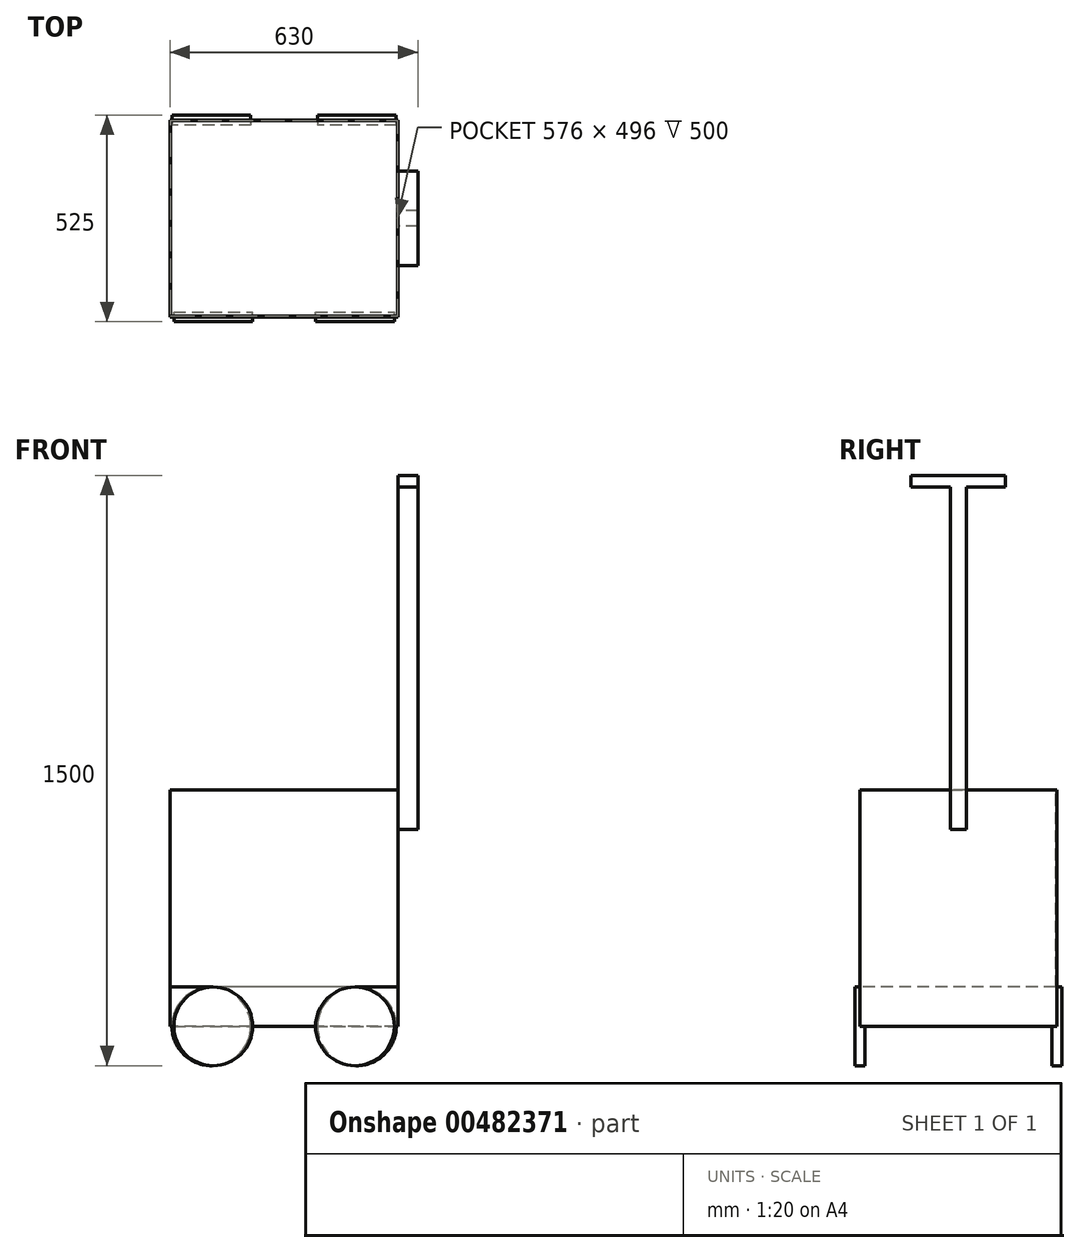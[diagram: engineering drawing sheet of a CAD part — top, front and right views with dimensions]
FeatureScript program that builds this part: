
annotation { "Feature Type Name" : "Feature", "Feature Type Description" : "" }
export const myFeature = defineFeature(function(context is Context, id is Id, definition is map)
    precondition{}
    {
        {
            var Q0;
            Q0=qCreatedBy(makeId("Front.planeOp"),FACE);
            var sketch = newSketch(context, id + "F0", { "sketchPlane" : qUnion([Q0])});
            skLineSegment(sketch, "E0.bottom", {"start": v(-288.14, 408.59) * mm, "end": v(291.86, 408.59) * mm});
            skLineSegment(sketch, "E0.top", {"start": v(-288.14, -191.41) * mm, "end": v(291.86, -191.41) * mm});
            skLineSegment(sketch, "E0.left", {"start": v(-288.14, 408.59) * mm, "end": v(-288.14, -191.41) * mm});
            skLineSegment(sketch, "E0.right", {"start": v(291.86, 408.59) * mm, "end": v(291.86, -191.41) * mm});
            skSolve(sketch);
        }
        {
            var Q0;
            Q0=makeQuery(id+"F0.imprint","IMPRINT",FACE,{"disambiguationData":[TD([[makeQuery(id+"F0.imprint","IMPRINT",EDGE,{"derivedFrom":sQuery(id+"F0.wireOp",EDGE,"E0.bottom")}),-1.0]])]});
            extrude(context, id + "F1", {"entities" : qUnion([Q0]), "depth" : 500 * mm});
        }
        {
            var Q0;
            Q0=makeQuery(id+"F1.opExtrude","SWEPT_FACE",FACE,{"disambiguationData":[OSD([sQuery(id+"F0.wireOp",EDGE,"E0.bottom")])]});
            var sketch = newSketch(context, id + "F2", { "sketchPlane" : qUnion([Q0])});
            skLineSegment(sketch, "E1.bottom", {"start": v(289.86, -2) * mm, "end": v(-286.14, -2) * mm});
            skLineSegment(sketch, "E1.top", {"start": v(289.86, -498) * mm, "end": v(-286.14, -498) * mm});
            skLineSegment(sketch, "E1.left", {"start": v(289.86, -2) * mm, "end": v(289.86, -498) * mm});
            skLineSegment(sketch, "E1.right", {"start": v(-286.14, -2) * mm, "end": v(-286.14, -498) * mm});
            skSolve(sketch);
        }
        {
            var Q0;
            Q0=makeQuery(id+"F2.imprint","IMPRINT",FACE,{"disambiguationData":[TD([[makeQuery(id+"F2.imprint","IMPRINT",EDGE,{"derivedFrom":sQuery(id+"F2.wireOp",EDGE,"E1.bottom")}),1.0]])]});
            extrude(context, id + "F3", {"entities" : qUnion([Q0]), "operationType" : NewBodyOperationType.REMOVE, "oppositeDirection" : true, "depth" : 500 * mm});
        }
        {
            var Q0;
            Q0=makeQuery(id+"F1.opExtrude","SWEPT_FACE",FACE,{"disambiguationData":[OSD([sQuery(id+"F0.wireOp",EDGE,"E0.right")])]});
            var sketch = newSketch(context, id + "F4", { "sketchPlane" : qUnion([Q0])});
            skPoint(sketch, "E2.oppositeSnap0", {"position": v(-250, 408.59) * mm});
            skLineSegment(sketch, "E3.bottom", {"start": v(-270, 308.59) * mm, "end": v(-230, 308.59) * mm});
            skLineSegment(sketch, "E3.top", {"start": v(-270, 1208.59) * mm, "end": v(-230, 1208.59) * mm});
            skLineSegment(sketch, "E3.left", {"start": v(-230, 308.59) * mm, "end": v(-230, 1208.59) * mm});
            skLineSegment(sketch, "E3.right", {"start": v(-270, 308.59) * mm, "end": v(-270, 1208.59) * mm});
            skSolve(sketch);
        }
        {
            var Q0;
            {var subQ0=sQuery(id+"F4.wireOp",EDGE,"E3.top");Q0=makeQuery(id+"F4.imprint","IMPRINT",FACE,{"disambiguationData":[TD([[makeQuery(id+"F4.imprint","IMPRINT",EDGE,{"derivedFrom":subQ0}),-1.0]])]});}
            var Q1;
            {var subQ0=sQuery(id+"F4.wireOp",EDGE,"E3.bottom");Q1=makeQuery(id+"F4.imprint","IMPRINT",FACE,{"disambiguationData":[TD([[makeQuery(id+"F4.imprint","IMPRINT",EDGE,{"derivedFrom":subQ0}),1.0]])]});}
            extrude(context, id + "F5", {"entities" : qUnion([Q0, Q1]), "operationType" : NewBodyOperationType.ADD, "depth" : 50 * mm});
        }
        {
            var Q0;
            Q0=makeQuery(id+"F5.opExtrude","SWEPT_FACE",FACE,{"disambiguationData":[OSD([sQuery(id+"F4.wireOp",EDGE,"E3.top")])]});
            var sketch = newSketch(context, id + "F6", { "sketchPlane" : qUnion([Q0])});
            skLineSegment(sketch, "E4.bottom", {"start": v(341.86, -130) * mm, "end": v(291.86, -130) * mm});
            skLineSegment(sketch, "E4.top", {"start": v(341.86, -370) * mm, "end": v(291.86, -370) * mm});
            skLineSegment(sketch, "E4.left", {"start": v(341.86, -130) * mm, "end": v(341.86, -370) * mm});
            skLineSegment(sketch, "E4.right", {"start": v(291.86, -130) * mm, "end": v(291.86, -370) * mm});
            skPoint(sketch, "E4.middle", {"position": v(316.86, -250) * mm});
            skPoint(sketch, "E4.middle.positionSnap0", {"position": v(291.86, -250) * mm});
            skPoint(sketch, "E4.centerSnap0", {"position": v(291.86, -250) * mm});
            skSolve(sketch);
        }
        {
            var Q0;
            {var subQ0=sQuery(id+"F6.wireOp",EDGE,"E4.top");Q0=makeQuery(id+"F6.imprint","IMPRINT",FACE,{"disambiguationData":[TD([[makeQuery(id+"F6.imprint","IMPRINT",EDGE,{"derivedFrom":subQ0}),-1.0]])]});}
            var Q1;
            {var subQ0=sQuery(id+"F6.wireOp",EDGE,"E4.bottom");Q1=makeQuery(id+"F6.imprint","IMPRINT",FACE,{"disambiguationData":[TD([[makeQuery(id+"F6.imprint","IMPRINT",EDGE,{"derivedFrom":subQ0}),1.0]])]});}
            extrude(context, id + "F7", {"entities" : qUnion([Q0, Q1]), "operationType" : NewBodyOperationType.ADD, "oppositeDirection" : true, "depth" : 30 * mm});
        }
        {
            var Q0;
            Q0=makeQuery(id+"F1.opExtrude","CAP_FACE",FACE,{"disambiguationData":[OSD([sQuery(id+"F0.wireOp",EDGE,"E0.bottom"),sQuery(id+"F0.wireOp",EDGE,"E0.top"),sQuery(id+"F0.wireOp",EDGE,"E0.left"),sQuery(id+"F0.wireOp",EDGE,"E0.right")])],"isStart":false});
            var sketch = newSketch(context, id + "F8", { "sketchPlane" : qUnion([Q0])});
            skCircle(sketch, "E5", {"center": v(-178.14, -191.41) * mm, "radius": 100 * mm});
            skCircle(sketch, "E6", {"center": v(181.86, -191.41) * mm, "radius": 100 * mm});
            skSolve(sketch);
        }
        {
            var Q0;
            {var subQ0=sQuery(id+"F8.wireOp",EDGE,"E5");var subQ1=makeQuery(id+"F1.opExtrude","CAP_EDGE",EDGE,{"disambiguationData":[OSD([sQuery(id+"F0.wireOp",EDGE,"E0.top")])],"isStart":false});var subQ2=makeQuery(id+"F8.imprint","INTERSECT",VERTEX,{"disambiguationData":[OD(0.0)],"derivedFrom":[subQ1,subQ0]});Q0=makeQuery(id+"F8.imprint","IMPRINT",FACE,{"disambiguationData":[TD([[makeQuery(id+"F8.imprint","IMPRINT",EDGE,{"disambiguationData":[TD([[subQ2,-1.0]])],"derivedFrom":subQ0}),1.0]])]});}
            var Q1;
            {var subQ0=sQuery(id+"F8.wireOp",EDGE,"E5");var subQ1=makeQuery(id+"F1.opExtrude","CAP_EDGE",EDGE,{"disambiguationData":[OSD([sQuery(id+"F0.wireOp",EDGE,"E0.top")])],"isStart":false});var subQ2=makeQuery(id+"F8.imprint","INTERSECT",VERTEX,{"disambiguationData":[OD(0.0)],"derivedFrom":[subQ1,subQ0]});Q1=makeQuery(id+"F8.imprint","IMPRINT",FACE,{"disambiguationData":[TD([[makeQuery(id+"F8.imprint","IMPRINT",EDGE,{"disambiguationData":[TD([[subQ2,1.0]])],"derivedFrom":subQ0}),1.0]])]});}
            var Q2;
            {var subQ0=sQuery(id+"F8.wireOp",EDGE,"E6");var subQ1=makeQuery(id+"F1.opExtrude","CAP_EDGE",EDGE,{"disambiguationData":[OSD([sQuery(id+"F0.wireOp",EDGE,"E0.top")])],"isStart":false});var subQ2=makeQuery(id+"F8.imprint","INTERSECT",VERTEX,{"disambiguationData":[OD(0.0)],"derivedFrom":[subQ1,subQ0]});Q2=makeQuery(id+"F8.imprint","IMPRINT",FACE,{"disambiguationData":[TD([[makeQuery(id+"F8.imprint","IMPRINT",EDGE,{"disambiguationData":[TD([[subQ2,1.0]])],"derivedFrom":subQ0}),1.0]])]});}
            var Q3;
            {var subQ0=sQuery(id+"F8.wireOp",EDGE,"E6");var subQ1=makeQuery(id+"F1.opExtrude","CAP_EDGE",EDGE,{"disambiguationData":[OSD([sQuery(id+"F0.wireOp",EDGE,"E0.top")])],"isStart":false});var subQ2=makeQuery(id+"F8.imprint","INTERSECT",VERTEX,{"disambiguationData":[OD(0.0)],"derivedFrom":[subQ1,subQ0]});Q3=makeQuery(id+"F8.imprint","IMPRINT",FACE,{"disambiguationData":[TD([[makeQuery(id+"F8.imprint","IMPRINT",EDGE,{"disambiguationData":[TD([[subQ2,-1.0]])],"derivedFrom":subQ0}),1.0]])]});}
            extrude(context, id + "F9", {"entities" : qUnion([Q0, Q1, Q2, Q3]), "operationType" : NewBodyOperationType.ADD, "endBound" : BoundingType.SYMMETRIC, "depth" : 25 * mm});
        }
        {
            var Q0;
            Q0=makeQuery(id+"F1.opExtrude","CAP_FACE",FACE,{"disambiguationData":[OSD([sQuery(id+"F0.wireOp",EDGE,"E0.bottom"),sQuery(id+"F0.wireOp",EDGE,"E0.top"),sQuery(id+"F0.wireOp",EDGE,"E0.left"),sQuery(id+"F0.wireOp",EDGE,"E0.right")])],"isStart":true});
            var sketch = newSketch(context, id + "F10", { "sketchPlane" : qUnion([Q0])});
            skCircle(sketch, "E7", {"center": v(-186.86, -191.41) * mm, "radius": 100 * mm});
            skCircle(sketch, "E8", {"center": v(183.14, -191.41) * mm, "radius": 100 * mm});
            skSolve(sketch);
        }
        {
            var Q0;
            {var subQ0=sQuery(id+"F10.wireOp",EDGE,"E7");var subQ1=makeQuery(id+"F1.opExtrude","CAP_EDGE",EDGE,{"disambiguationData":[OSD([sQuery(id+"F0.wireOp",EDGE,"E0.top")])],"isStart":true});var subQ2=makeQuery(id+"F10.imprint","INTERSECT",VERTEX,{"disambiguationData":[OD(0.0)],"derivedFrom":[subQ1,subQ0]});Q0=makeQuery(id+"F10.imprint","IMPRINT",FACE,{"disambiguationData":[TD([[makeQuery(id+"F10.imprint","IMPRINT",EDGE,{"disambiguationData":[TD([[subQ2,-1.0]])],"derivedFrom":subQ0}),1.0]])]});}
            var Q1;
            {var subQ0=sQuery(id+"F10.wireOp",EDGE,"E7");var subQ1=makeQuery(id+"F1.opExtrude","CAP_EDGE",EDGE,{"disambiguationData":[OSD([sQuery(id+"F0.wireOp",EDGE,"E0.top")])],"isStart":true});var subQ2=makeQuery(id+"F10.imprint","INTERSECT",VERTEX,{"disambiguationData":[OD(0.0)],"derivedFrom":[subQ1,subQ0]});Q1=makeQuery(id+"F10.imprint","IMPRINT",FACE,{"disambiguationData":[TD([[makeQuery(id+"F10.imprint","IMPRINT",EDGE,{"disambiguationData":[TD([[subQ2,1.0]])],"derivedFrom":subQ0}),1.0]])]});}
            var Q2;
            {var subQ0=sQuery(id+"F10.wireOp",EDGE,"E8");var subQ1=makeQuery(id+"F1.opExtrude","CAP_EDGE",EDGE,{"disambiguationData":[OSD([sQuery(id+"F0.wireOp",EDGE,"E0.top")])],"isStart":true});var subQ2=makeQuery(id+"F10.imprint","INTERSECT",VERTEX,{"disambiguationData":[OD(0.0)],"derivedFrom":[subQ1,subQ0]});Q2=makeQuery(id+"F10.imprint","IMPRINT",FACE,{"disambiguationData":[TD([[makeQuery(id+"F10.imprint","IMPRINT",EDGE,{"disambiguationData":[TD([[subQ2,1.0]])],"derivedFrom":subQ0}),1.0]])]});}
            var Q3;
            {var subQ0=sQuery(id+"F10.wireOp",EDGE,"E8");var subQ1=makeQuery(id+"F1.opExtrude","CAP_EDGE",EDGE,{"disambiguationData":[OSD([sQuery(id+"F0.wireOp",EDGE,"E0.top")])],"isStart":true});var subQ2=makeQuery(id+"F10.imprint","INTERSECT",VERTEX,{"disambiguationData":[OD(0.0)],"derivedFrom":[subQ1,subQ0]});Q3=makeQuery(id+"F10.imprint","IMPRINT",FACE,{"disambiguationData":[TD([[makeQuery(id+"F10.imprint","IMPRINT",EDGE,{"disambiguationData":[TD([[subQ2,-1.0]])],"derivedFrom":subQ0}),1.0]])]});}
            extrude(context, id + "F11", {"entities" : qUnion([Q0, Q1, Q2, Q3]), "operationType" : NewBodyOperationType.ADD, "endBound" : BoundingType.SYMMETRIC, "depth" : 25 * mm});
        }
    });
